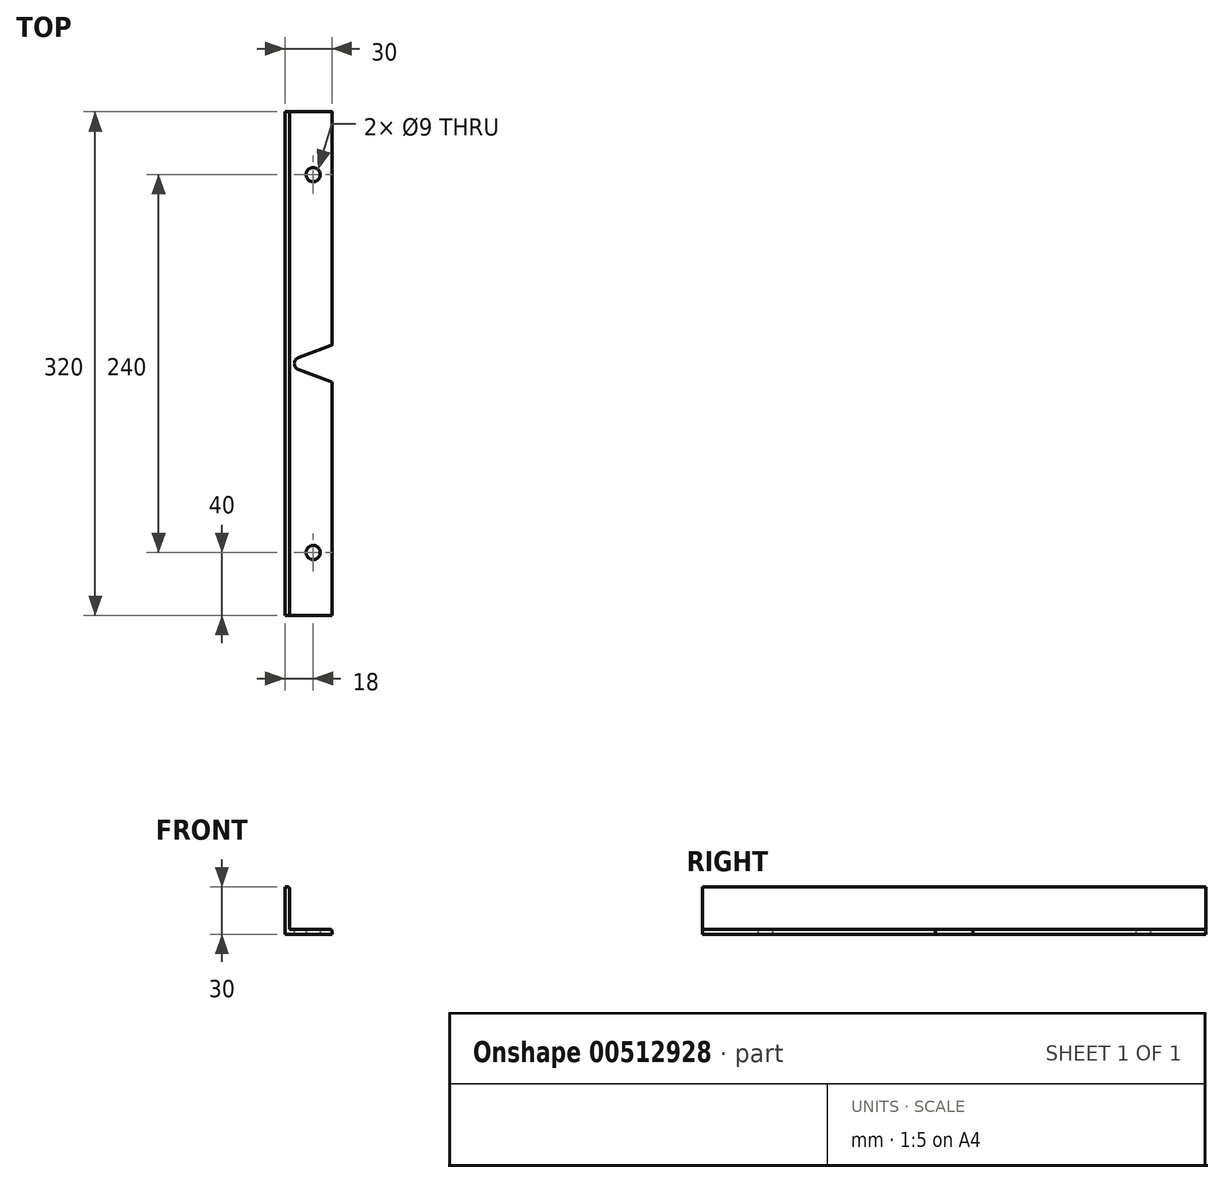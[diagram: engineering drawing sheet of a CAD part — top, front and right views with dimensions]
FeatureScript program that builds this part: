
annotation { "Feature Type Name" : "Feature", "Feature Type Description" : "" }
export const myFeature = defineFeature(function(context is Context, id is Id, definition is map)
    precondition{}
    {
        {
            var Q0;
            Q0=qCreatedBy(makeId("Front.planeOp"),FACE);
            var sketch = newSketch(context, id + "F0", { "sketchPlane" : qUnion([Q0])});
            skLineSegment(sketch, "E0", {"start": v(0, 0) * mm, "end": v(30, 0) * mm});
            skLineSegment(sketch, "E1", {"start": v(30, 0) * mm, "end": v(30, 2) * mm});
            skLineSegment(sketch, "E2", {"start": v(29, 3) * mm, "end": v(4, 3) * mm});
            skLineSegment(sketch, "E3", {"start": v(3, 4) * mm, "end": v(3, 29) * mm});
            skLineSegment(sketch, "E4", {"start": v(2, 30) * mm, "end": v(0, 30) * mm});
            skLineSegment(sketch, "E5", {"start": v(0, 30) * mm, "end": v(0, 0) * mm});
            skPoint(sketch, "E6.visualSharp", {"position": v(3, 3) * mm});
            skArc(sketch, "E6.filletArc", {"start": v(3, 4) * mm, "mid": v(3.3, 3.3) * mm, "end": v(4, 3) * mm});
            skPoint(sketch, "E7.visualSharp", {"position": v(30, 3) * mm});
            skArc(sketch, "E7.filletArc", {"start": v(30, 2) * mm, "mid": v(29.7, 2.7) * mm, "end": v(29, 3) * mm});
            skPoint(sketch, "E8.visualSharp", {"position": v(3, 30) * mm});
            skArc(sketch, "E8.filletArc", {"start": v(3, 29) * mm, "mid": v(2.7, 29.7) * mm, "end": v(2, 30) * mm});
            skSolve(sketch);
        }
        {
            var Q0;
            Q0 = qSketchRegion(id + "F0", true);
            extrude(context, id + "F1", {"entities" : qUnion([Q0]), "depth" : 320 * mm});
        }
        {
            var Q0;
            Q0=qCreatedBy(makeId("Top.planeOp"),FACE);
            var sketch = newSketch(context, id + "F2", { "sketchPlane" : qUnion([Q0])});
            skPoint(sketch, "E9", {"position": v(18, -40) * mm});
            skPoint(sketch, "E10", {"position": v(18, -280) * mm});
            skLineSegment(sketch, "E11", {"start": v(-34.86, -160) * mm, "end": v(149.07, -160) * mm, "construction": true});
            skArc(sketch, "E12", {"start": v(8.59, -156.26) * mm, "mid": v(6.71, -157.72) * mm, "end": v(6, -160) * mm});
            skLineSegment(sketch, "E13", {"start": v(8.59, -156.26) * mm, "end": v(30, -148.18) * mm});
            skLineSegment(sketch, "E14", {"start": v(30, -148.18) * mm, "end": v(30, -160) * mm});
            skArc(sketch, "E15.MirrorCS", {"start": v(8.59, -163.74) * mm, "mid": v(6.71, -162.28) * mm, "end": v(6, -160) * mm});
            skLineSegment(sketch, "E16.MirrorCS", {"start": v(8.59, -163.74) * mm, "end": v(30, -171.82) * mm});
            skLineSegment(sketch, "E17.MirrorCS", {"start": v(30, -171.82) * mm, "end": v(30, -160) * mm});
            skSolve(sketch);
        }
        {
            var Q0;
            Q0 = qSketchRegion(id + "F2", true);
            var Q1;
            Q1=makeQuery(id+"F1.opExtrude","SWEPT_FACE",FACE,{"disambiguationData":[OSD([sQuery(id+"F0.wireOp",EDGE,"E4")])]});
            extrude(context, id + "F3", {"entities" : qUnion([Q0]), "operationType" : NewBodyOperationType.REMOVE, "endBound" : BoundingType.UP_TO_SURFACE, "endBoundEntityFace" : qUnion([Q1]), "depth" : 25 * mm});
        }
        {
            var Q0;
            Q0=sQuery(id+"F2.wireOp",VERTEX,"E9");
            var Q1;
            Q1=sQuery(id+"F2.wireOp",VERTEX,"E10");
            var Q2;
            Q2=makeQuery(id+"F1.opExtrude","SWEPT_BODY",BODY,{"disambiguationData":[OSD([sQuery(id+"F0.wireOp",EDGE,"E0"),sQuery(id+"F0.wireOp",EDGE,"E1"),sQuery(id+"F0.wireOp",EDGE,"E2"),sQuery(id+"F0.wireOp",EDGE,"E3"),sQuery(id+"F0.wireOp",EDGE,"E4"),sQuery(id+"F0.wireOp",EDGE,"E5"),sQuery(id+"F0.wireOp",EDGE,"E6.filletArc"),sQuery(id+"F0.wireOp",EDGE,"E7.filletArc"),sQuery(id+"F0.wireOp",EDGE,"E8.filletArc")])]});
            hole(context, id + "F4", {"style" : HoleStyle.SIMPLE, "endStyle" : HoleEndStyle.THROUGH, "oppositeDirection" : true, "standardTappedOrClearance" : lookupTablePath({ "standard" : "ISO", "size" : "9", "type" : "Drilled" }), "standardBlindInLast" : lookupTablePath({ "standard" : "ISO", "size" : "9", "type" : "Drilled" }), "holeDiameter" : 9 * mm, "isTappedThrough" : true, "tappedDepth" : 12 * mm, "tapClearance" : 3, "locations" : qUnion([Q0, Q1]), "scope" : qUnion([Q2])});
        }
    });
